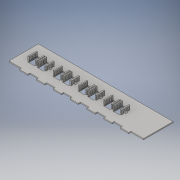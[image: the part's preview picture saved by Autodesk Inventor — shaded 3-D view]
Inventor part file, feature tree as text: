
AUTODESK INVENTOR PART (.ipt)
format: ipt  version: 2016 (Build 200138000, 138)  size: 393,728 bytes
history: native  units: in
note: dims shown in document units (in); Inventor stores cm internally (conversion verified against a paired STEP export)
features: extrude x5, sketch x5, chamfer x1, fillet x1
ambient origin geometry x8: Origin, YZ Plane, XZ Plane, XY Plane, X Axis, Y Axis, Z Axis, Center Point
bodies: Solid1 (feature_tree)
feature tree (12):
  extrude  "Extrusion1"  Depth=0.125in TaperAngle=0.0deg
  extrude  "Extrusion2"  Depth=0.125in TaperAngle=0.0deg
  extrude  "Extrusion4"  Depth=0.3937in
  extrude  "Extrusion5"  Depth=0.5in TaperAngle=0.0deg
  chamfer  "Chamfer1"  Distance=16.0in
  fillet  "Fillet1"  Radius=0.125in
  sketch  "Sketch1"  dims[d0=16.0in d1=3.5in d2=0.125in d3=0.0in]
  sketch  "Sketch3"  dims[d5=2.7559in d7=0.3937in d8=2.0in d9=1.0in d10=0.125in d11=0.0in]
  sketch  "Sketch5"  dims[d22=1.5748in d24=3.0in d25=0.3937in d27=1.0in d29=0.5in d30=0.0in d31=16.0in d32=0.0in]
  sketch  "Sketch6"  dims[d33=0.125in d34=0.125in d35=45.0deg d36=0.125in]
  extrude  "Extrusion3"  [1 undecoded]
  sketch  "Sketch4"  dims[d12=1.0in d13=3.0in d15=0.3937in d17=1.5748in d19=0.0in d20=0.1969in d21=0.1969in]
note: 1 required parameter value undecoded (feature->parameter linkage not recoverable at this tier; creation-order binding heuristic only, values carry confidence <= 0.55)
